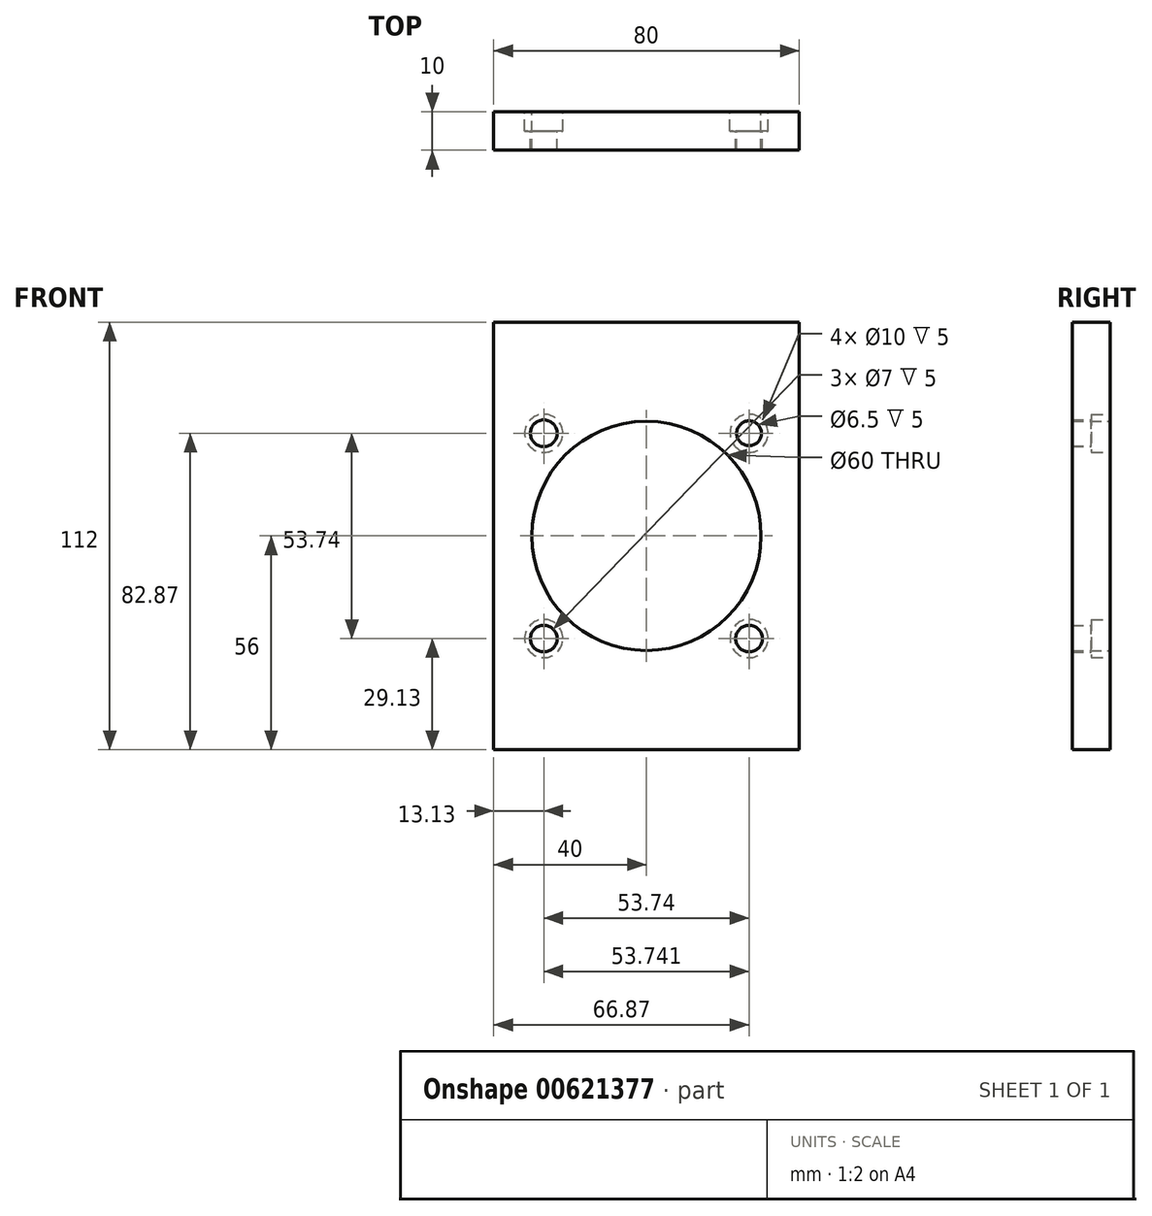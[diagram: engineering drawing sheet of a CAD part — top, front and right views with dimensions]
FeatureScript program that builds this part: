
annotation { "Feature Type Name" : "Feature", "Feature Type Description" : "" }
export const myFeature = defineFeature(function(context is Context, id is Id, definition is map)
    precondition{}
    {
        {
            var Q0;
            Q0=qCreatedBy(makeId("Front.planeOp"),FACE);
            var sketch = newSketch(context, id + "F0", { "sketchPlane" : qUnion([Q0])});
            skCircle(sketch, "E0", {"center": v(26.87, 26.87) * mm, "radius": 3.25 * mm});
            skCircle(sketch, "E1", {"center": v(-26.87, 26.87) * mm, "radius": 3.5 * mm});
            skCircle(sketch, "E2", {"center": v(26.87, -26.87) * mm, "radius": 3.5 * mm});
            skCircle(sketch, "E3", {"center": v(-26.87, -26.87) * mm, "radius": 3.5 * mm});
            skCircle(sketch, "E4", {"center": v(0, 0) * mm, "radius": 30 * mm});
            skLineSegment(sketch, "E5.bottom", {"start": v(40, 56) * mm, "end": v(-40, 56) * mm});
            skLineSegment(sketch, "E5.top", {"start": v(40, -56) * mm, "end": v(-40, -56) * mm});
            skLineSegment(sketch, "E5.left", {"start": v(40, 56) * mm, "end": v(40, -56) * mm});
            skLineSegment(sketch, "E5.right", {"start": v(-40, 56) * mm, "end": v(-40, -56) * mm});
            skSolve(sketch);
        }
        {
            var Q0;
            Q0 = qSketchRegion(id + "F0", true);
            extrude(context, id + "F1", {"entities" : qUnion([Q0]), "depth" : 10 * mm, "offsetDistance" : 25 * mm});
        }
        {
            var Q0;
            Q0=makeQuery(id+"F1.opExtrude","CAP_FACE",FACE,{"disambiguationData":[OSD([sQuery(id+"F0.wireOp",EDGE,"E0"),sQuery(id+"F0.wireOp",EDGE,"E1"),sQuery(id+"F0.wireOp",EDGE,"E2"),sQuery(id+"F0.wireOp",EDGE,"E3"),sQuery(id+"F0.wireOp",EDGE,"E4"),sQuery(id+"F0.wireOp",EDGE,"E5.bottom"),sQuery(id+"F0.wireOp",EDGE,"E5.top"),sQuery(id+"F0.wireOp",EDGE,"E5.left"),sQuery(id+"F0.wireOp",EDGE,"E5.right")])],"isStart":true});
            var sketch = newSketch(context, id + "F2", { "sketchPlane" : qUnion([Q0])});
            skCircle(sketch, "E6", {"center": v(-26.87, 26.87) * mm, "radius": 5 * mm});
            skCircle(sketch, "E7", {"center": v(-26.87, -26.87) * mm, "radius": 5 * mm});
            skCircle(sketch, "E8", {"center": v(26.87, -26.87) * mm, "radius": 5 * mm});
            skCircle(sketch, "E9", {"center": v(26.87, 26.87) * mm, "radius": 5 * mm});
            skSolve(sketch);
        }
        {
            var Q0;
            Q0=makeQuery(id+"F2.imprint","IMPRINT",FACE,{"disambiguationData":[TD([[makeQuery(id+"F2.imprint","IMPRINT",EDGE,{"derivedFrom":sQuery(id+"F2.wireOp",EDGE,"E6")}),1.0]])]});
            var Q1;
            Q1=makeQuery(id+"F2.imprint","IMPRINT",FACE,{"disambiguationData":[TD([[makeQuery(id+"F2.imprint","IMPRINT",EDGE,{"derivedFrom":sQuery(id+"F2.wireOp",EDGE,"E9")}),1.0]])]});
            var Q2;
            Q2=makeQuery(id+"F2.imprint","IMPRINT",FACE,{"disambiguationData":[TD([[makeQuery(id+"F2.imprint","IMPRINT",EDGE,{"derivedFrom":sQuery(id+"F2.wireOp",EDGE,"E8")}),1.0]])]});
            var Q3;
            Q3=makeQuery(id+"F2.imprint","IMPRINT",FACE,{"disambiguationData":[TD([[makeQuery(id+"F2.imprint","IMPRINT",EDGE,{"derivedFrom":sQuery(id+"F2.wireOp",EDGE,"E7")}),1.0]])]});
            extrude(context, id + "F3", {"entities" : qUnion([Q0, Q1, Q2, Q3]), "operationType" : NewBodyOperationType.REMOVE, "oppositeDirection" : true, "depth" : 5 * mm, "offsetDistance" : 25 * mm});
        }
    });
